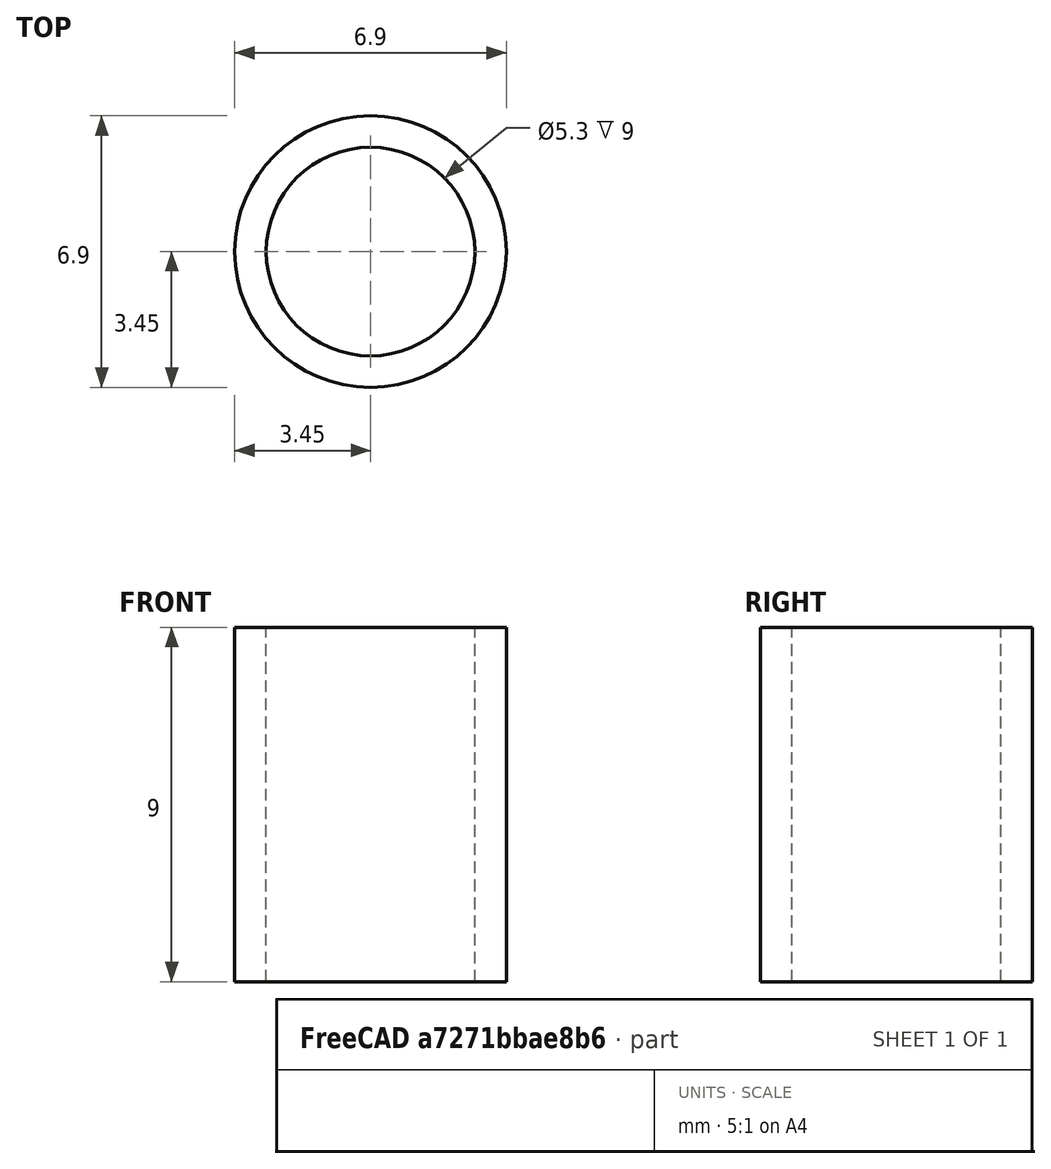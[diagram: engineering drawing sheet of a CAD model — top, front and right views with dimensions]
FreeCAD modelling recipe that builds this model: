
FCSTD DOCUMENT  (FreeCAD 0.18R16093 (Git))
Label: board_fan_spacer
License: All rights reserved
LicenseURL: http://en.wikipedia.org/wiki/All_rights_reserved
objects: PartDesign::AdditiveCylinder×1, Spreadsheet::Sheet×1, PartDesign::SubtractiveCylinder×1, PartDesign::Body×1
note: 5 computed .brp shape members not serialized (recipe doc carries the construction recipe); baked Part::Feature solids carry a one-line shape summary decoded from their .brp

FEATURE [PartDesign::AdditiveCylinder] Cylinder
  Angle = 360
  AttacherType = Attacher::AttachEngine3D
  Height = 9
  Radius = 3.45
  expr: Radius = var.d / 2
FEATURE [Spreadsheet::Sheet] Spreadsheet  label="var"
  cells = A1=d; B1(d)=6.9; A2=line_width; B2(line_width)=0.8
FEATURE [PartDesign::SubtractiveCylinder] Cylinder001
  Angle = 360
  AttacherType = Attacher::AttachEngine3D
  BaseFeature = -> Cylinder
  Height = 9
  Radius = 2.65
  expr: Radius = var.d / 2 - var.line_width
FEATURE [PartDesign::Body] Body
  Group = -> [Cylinder,Cylinder001]
  Origin = -> Origin
  Tip = -> Cylinder001
